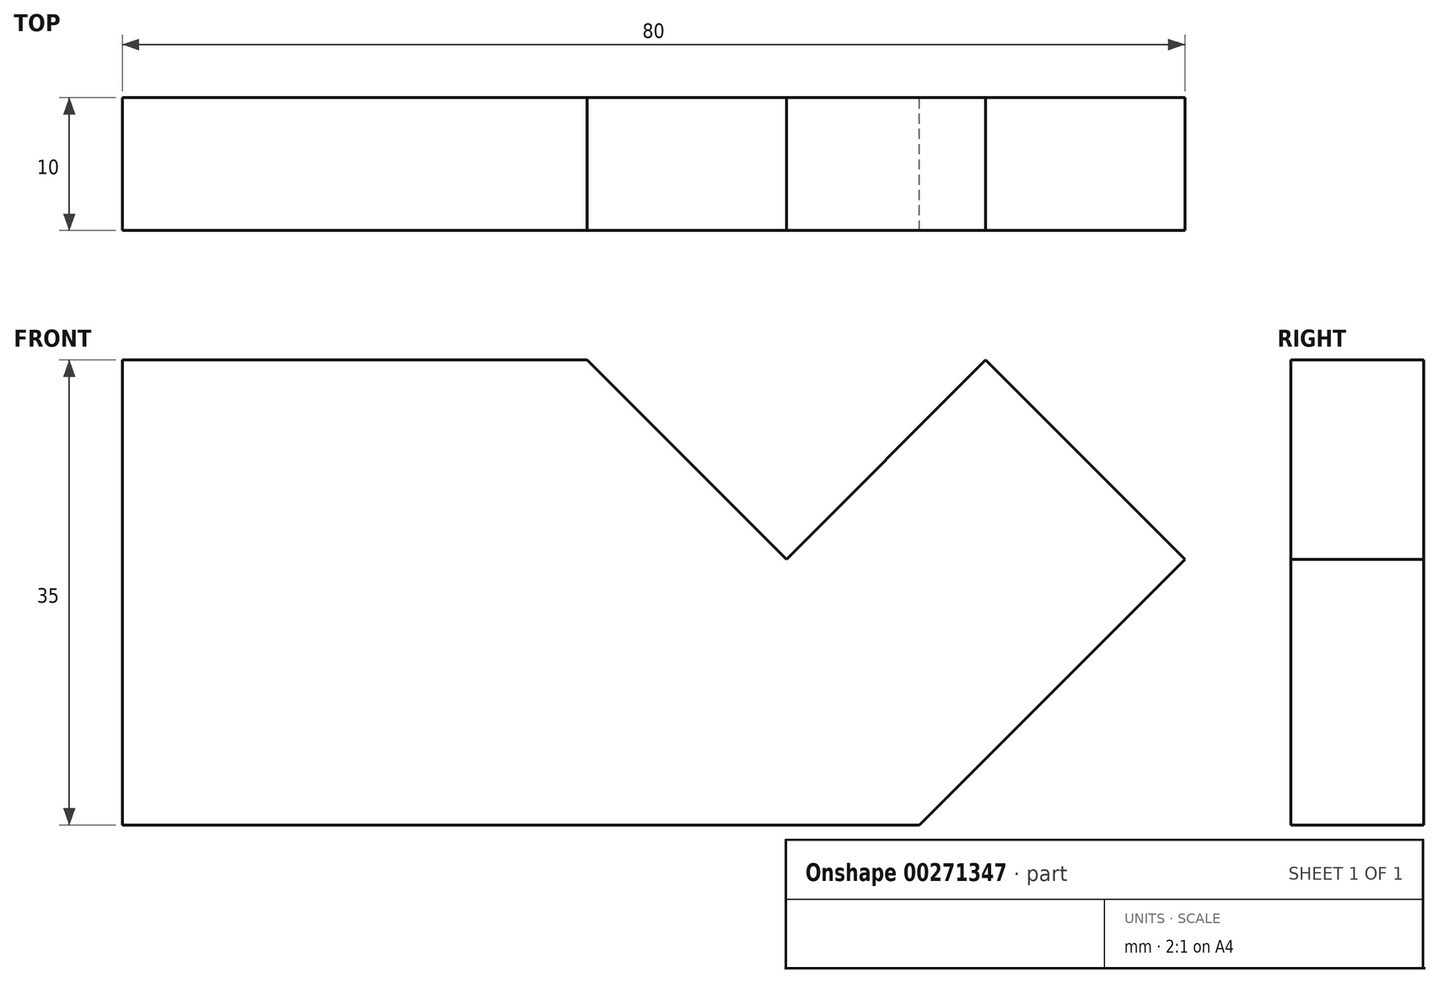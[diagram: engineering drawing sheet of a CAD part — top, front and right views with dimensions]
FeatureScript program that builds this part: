
annotation { "Feature Type Name" : "Feature", "Feature Type Description" : "" }
export const myFeature = defineFeature(function(context is Context, id is Id, definition is map)
    precondition{}
    {
        {
            var Q0;
            Q0=qCreatedBy(makeId("Front.planeOp"),FACE);
            var sketch = newSketch(context, id + "F0", { "sketchPlane" : qUnion([Q0])});
            skLineSegment(sketch, "E0", {"start": v(0, 0) * mm, "end": v(0, 35) * mm});
            skLineSegment(sketch, "E1", {"start": v(0, 0) * mm, "end": v(60, 0) * mm});
            skLineSegment(sketch, "E2", {"start": v(0, 35) * mm, "end": v(35, 35) * mm});
            skLineSegment(sketch, "E3", {"start": v(35, 35) * mm, "end": v(50, 20) * mm});
            skLineSegment(sketch, "E4", {"start": v(50, 20) * mm, "end": v(65, 35) * mm});
            skLineSegment(sketch, "E5", {"start": v(65, 35) * mm, "end": v(80, 20) * mm});
            skLineSegment(sketch, "E6", {"start": v(80, 20) * mm, "end": v(60, 0) * mm});
            skSolve(sketch);
        }
        {
            var Q0;
            Q0 = qSketchRegion(id + "F0", true);
            extrude(context, id + "F1", {"entities" : qUnion([Q0]), "depth" : 10 * mm});
        }
    });
